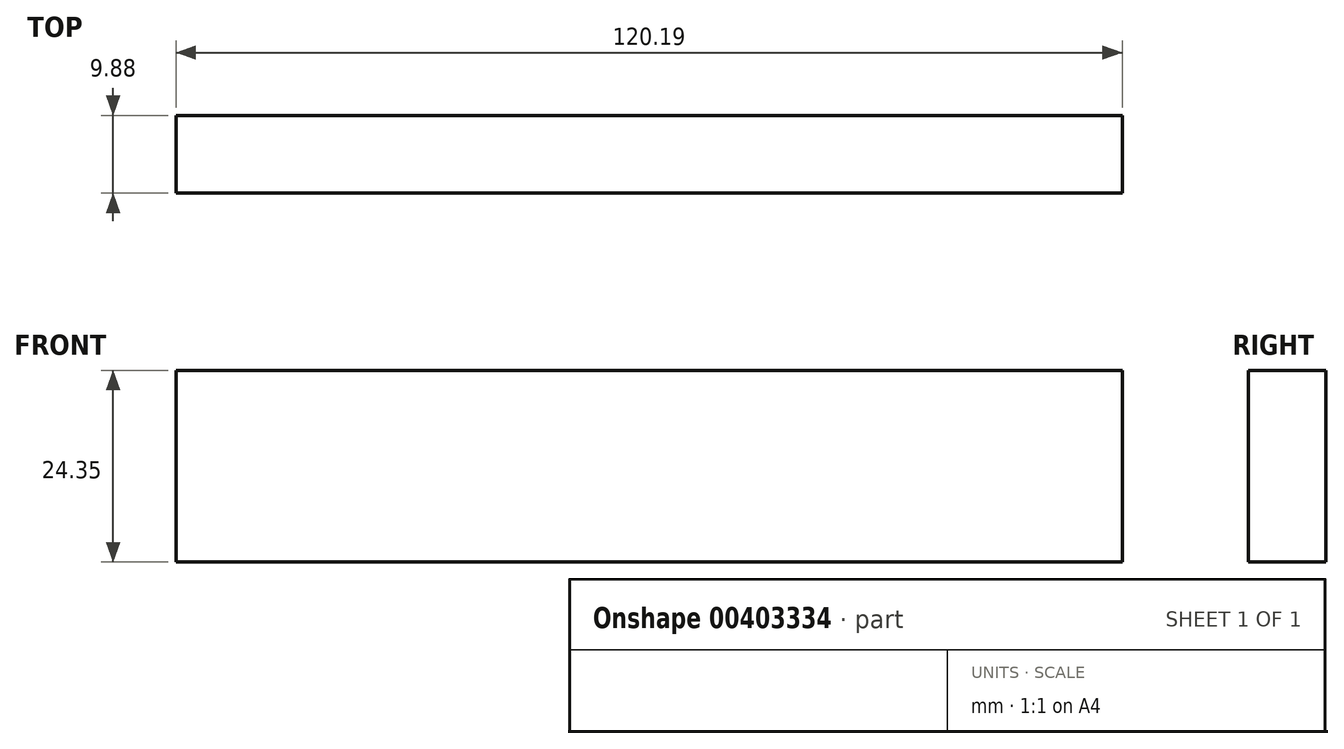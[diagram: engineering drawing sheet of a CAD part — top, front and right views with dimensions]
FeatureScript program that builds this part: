
annotation { "Feature Type Name" : "Feature", "Feature Type Description" : "" }
export const myFeature = defineFeature(function(context is Context, id is Id, definition is map)
    precondition{}
    {
        {
            var Q0;
            Q0=qCreatedBy(makeId("Front.planeOp"),FACE);
            var sketch = newSketch(context, id + "F0", { "sketchPlane" : qUnion([Q0])});
            skLineSegment(sketch, "E0.bottom", {"start": v(-17.32, 16.48) * mm, "end": v(-137.5, 16.48) * mm});
            skLineSegment(sketch, "E0.top", {"start": v(-17.32, 40.83) * mm, "end": v(-137.5, 40.83) * mm});
            skLineSegment(sketch, "E0.left", {"start": v(-17.32, 16.48) * mm, "end": v(-17.32, 40.83) * mm});
            skLineSegment(sketch, "E0.right", {"start": v(-137.5, 16.48) * mm, "end": v(-137.5, 40.83) * mm});
            skSolve(sketch);
        }
        {
            var Q0;
            Q0 = qSketchRegion(id + "F0", true);
            extrude(context, id + "F1", {"entities" : qUnion([Q0]), "depth" : 9.88 * mm});
        }
    });
